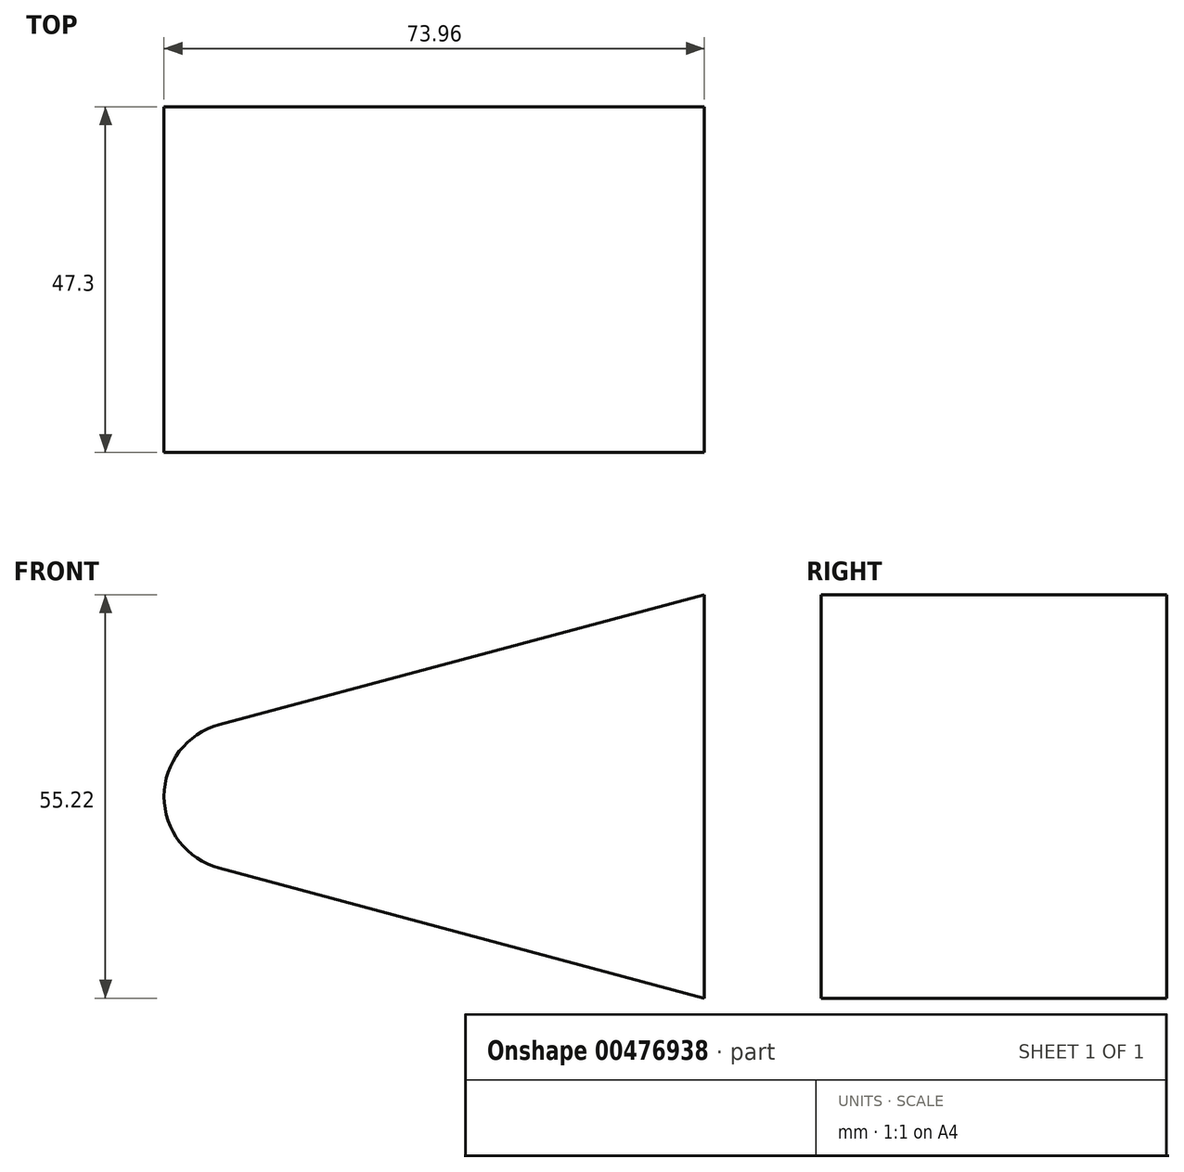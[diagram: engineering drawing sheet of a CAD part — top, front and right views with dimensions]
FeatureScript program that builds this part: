
annotation { "Feature Type Name" : "Feature", "Feature Type Description" : "" }
export const myFeature = defineFeature(function(context is Context, id is Id, definition is map)
    precondition{}
    {
        {
            var Q0;
            Q0=qCreatedBy(makeId("Front.planeOp"),FACE);
            var sketch = newSketch(context, id + "F0", { "sketchPlane" : qUnion([Q0])});
            skArc(sketch, "E0", {"start": v(22.77, 35.21) * mm, "mid": v(15.24, 25.4) * mm, "end": v(22.77, 15.59) * mm});
            skLineSegment(sketch, "E1", {"start": v(22.77, 35.21) * mm, "end": v(89.2, 53.01) * mm});
            skLineSegment(sketch, "E2", {"start": v(89.2, 53.01) * mm, "end": v(89.2, -2.21) * mm});
            skLineSegment(sketch, "E3", {"start": v(89.2, -2.21) * mm, "end": v(89.2, -2.21) * mm});
            skLineSegment(sketch, "E4", {"start": v(22.77, 15.59) * mm, "end": v(89.2, -2.21) * mm});
            skSolve(sketch);
        }
        {
            var Q0;
            Q0=makeQuery(id+"F0.imprint","IMPRINT",FACE,{"disambiguationData":[TD([[makeQuery(id+"F0.imprint","IMPRINT",EDGE,{"derivedFrom":sQuery(id+"F0.wireOp",EDGE,"E0")}),1.0]])]});
            extrude(context, id + "F1", {"entities" : qUnion([Q0]), "depth" : 47.3 * mm});
        }
    });
